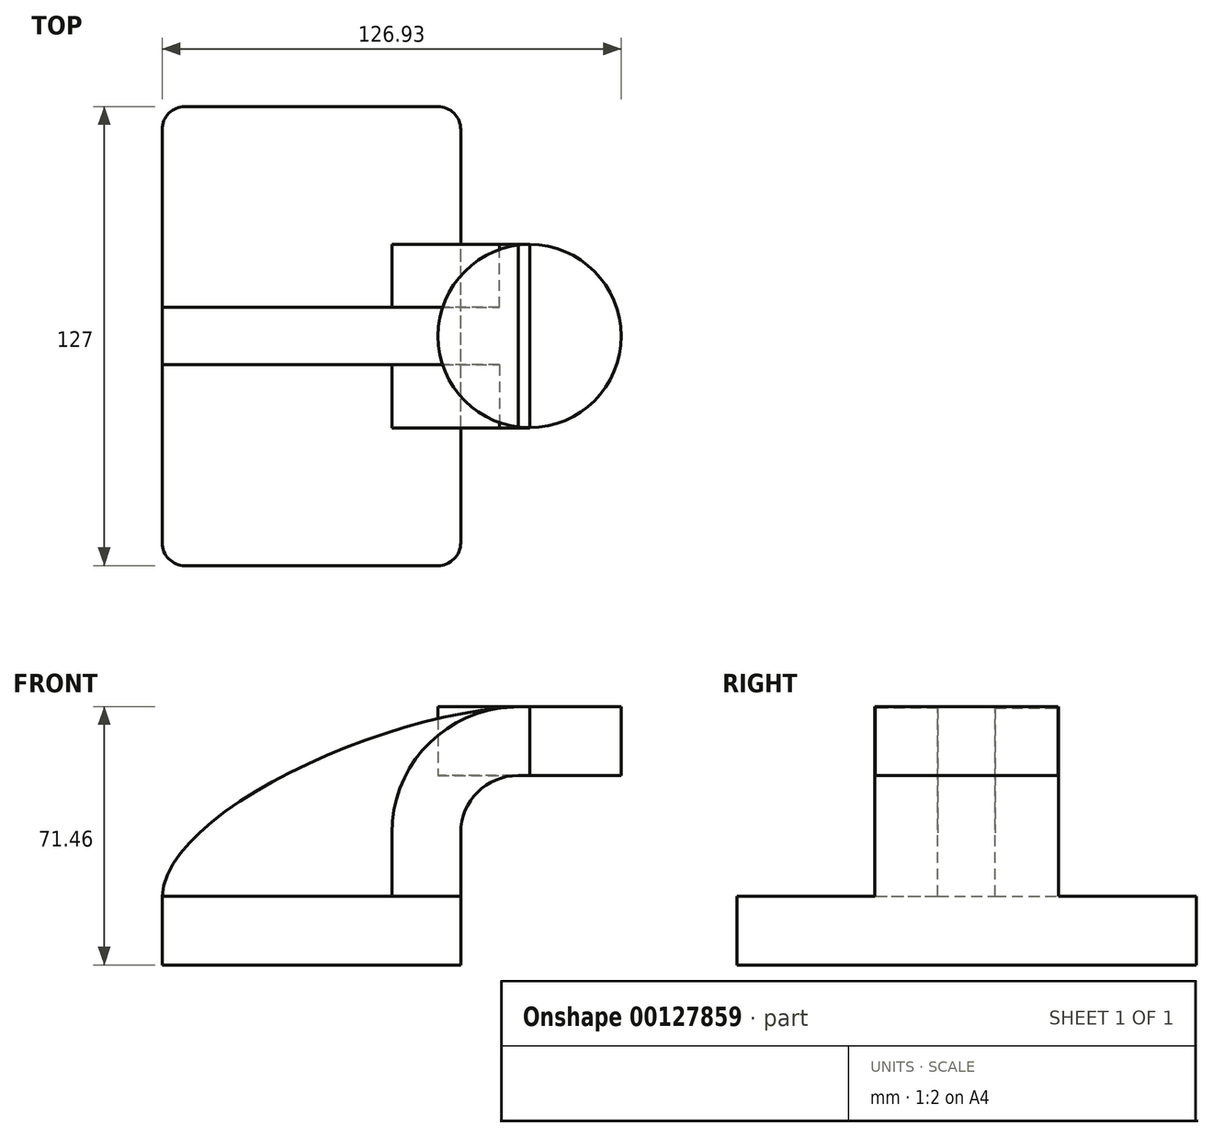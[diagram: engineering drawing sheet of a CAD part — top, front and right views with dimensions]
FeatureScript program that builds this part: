
annotation { "Feature Type Name" : "Feature", "Feature Type Description" : "" }
export const myFeature = defineFeature(function(context is Context, id is Id, definition is map)
    precondition{}
    {
        {
            var Q0;
            Q0=qCreatedBy(makeId("Front.planeOp"),FACE);
            var sketch = newSketch(context, id + "F0", { "sketchPlane" : qUnion([Q0])});
            skLineSegment(sketch, "E0.bottom", {"start": v(111.12, 38.1) * mm, "end": v(60.33, 38.1) * mm});
            skLineSegment(sketch, "E0.top", {"start": v(111.12, 66.68) * mm, "end": v(60.33, 66.68) * mm});
            skLineSegment(sketch, "E0.left", {"start": v(111.12, 38.1) * mm, "end": v(111.12, 66.68) * mm});
            skLineSegment(sketch, "E0.right", {"start": v(60.33, 38.1) * mm, "end": v(60.33, 66.68) * mm});
            skPoint(sketch, "E0.middle", {"position": v(85.72, 52.39) * mm});
            skLineSegment(sketch, "E1.bottom", {"start": v(41.28, -9.52) * mm, "end": v(-41.28, -9.53) * mm});
            skLineSegment(sketch, "E1.top", {"start": v(41.28, 9.53) * mm, "end": v(-41.28, 9.52) * mm});
            skLineSegment(sketch, "E1.left", {"start": v(41.28, -9.52) * mm, "end": v(41.28, 9.53) * mm});
            skLineSegment(sketch, "E1.right", {"start": v(-41.28, -9.53) * mm, "end": v(-41.28, 9.52) * mm});
            skPoint(sketch, "E1.middle", {"position": v(0, 0) * mm});
            skLineSegment(sketch, "E2", {"start": v(41.28, 9.53) * mm, "end": v(41.28, 27) * mm});
            skArc(sketch, "E3", {"start": v(41.28, 27) * mm, "mid": v(45.92, 38.23) * mm, "end": v(57.15, 42.88) * mm});
            skArc(sketch, "E4.1", {"start": v(22.23, 27) * mm, "mid": v(32.45, 51.7) * mm, "end": v(57.15, 61.93) * mm});
            skLineSegment(sketch, "E4.2", {"start": v(22.23, 9.53) * mm, "end": v(22.23, 27) * mm});
            skLineSegment(sketch, "E5", {"start": v(57.15, 42.88) * mm, "end": v(85.65, 42.88) * mm});
            skLineSegment(sketch, "E6", {"start": v(57.15, 61.93) * mm, "end": v(85.65, 61.93) * mm});
            skLineSegment(sketch, "E7", {"start": v(85.65, 61.93) * mm, "end": v(85.65, 42.88) * mm});
            skFitSpline(sketch, "E8", {"points": [v(-41.28, 9.53) * mm, v(57.15, 61.93) * mm], "startDerivative": vector(2.82, 69.45) * mm, "endDerivative": vector(112.7, 5.21) * mm});
            skSolve(sketch);
        }
        {
            var Q0;
            Q0=makeQuery(id+"F0.imprint","IMPRINT",FACE,{"disambiguationData":[TD([[makeQuery(id+"F0.imprint","IMPRINT",EDGE,{"derivedFrom":sQuery(id+"F0.wireOp",EDGE,"E1.bottom")}),-1.0]])]});
            extrude(context, id + "F1", {"entities" : qUnion([Q0]), "endBound" : BoundingType.SYMMETRIC, "depth" : 127 * mm});
        }
        {
            var Q0;
            {var subQ4=sQuery(id+"F0.wireOp",EDGE,"E2");Q0=makeQuery(id+"F0.imprint","IMPRINT",FACE,{"disambiguationData":[TD([[makeQuery(id+"F0.imprint","IMPRINT",EDGE,{"derivedFrom":subQ4}),1.0]])]});}
            extrude(context, id + "F2", {"entities" : qUnion([Q0]), "operationType" : NewBodyOperationType.ADD, "endBound" : BoundingType.SYMMETRIC, "depth" : 50.8 * mm});
        }
        {
            var Q0;
            {var subQ3=sQuery(id+"F0.wireOp",EDGE,"E4.2");Q0=makeQuery(id+"F0.imprint","IMPRINT",FACE,{"disambiguationData":[TD([[makeQuery(id+"F0.imprint","IMPRINT",EDGE,{"derivedFrom":subQ3}),1.0]])]});}
            extrude(context, id + "F3", {"entities" : qUnion([Q0]), "operationType" : NewBodyOperationType.ADD, "endBound" : BoundingType.SYMMETRIC, "depth" : 15.88 * mm});
        }
        {
            var Q0;
            {var subQ5=sQuery(id+"F0.wireOp",EDGE,"E7");Q0=makeQuery(id+"F0.imprint","IMPRINT",FACE,{"disambiguationData":[TD([[makeQuery(id+"F0.imprint","IMPRINT",EDGE,{"derivedFrom":subQ5}),-1.0]])]});}
            var Q1;
            Q1=sQuery(id+"F0.wireOp",EDGE,"E0.right");
            revolve(context, id + "F4", {"entities" : qUnion([Q0]), "axis" : qUnion([Q1]), "revolveType" : RevolveType.FULL});
        }
        {
            var Q0;
            Q0=makeQuery(id+"F1.opExtrude","CAP_EDGE",EDGE,{"disambiguationData":[OSD([sQuery(id+"F0.wireOp",EDGE,"E1.left")])],"isStart":true});
            var Q1;
            Q1=makeQuery(id+"F1.opExtrude","CAP_EDGE",EDGE,{"disambiguationData":[OSD([sQuery(id+"F0.wireOp",EDGE,"E1.left")])],"isStart":false});
            var Q2;
            Q2=makeQuery(id+"F1.opExtrude","CAP_EDGE",EDGE,{"disambiguationData":[OSD([sQuery(id+"F0.wireOp",EDGE,"E1.right")])],"isStart":false});
            var Q3;
            Q3=makeQuery(id+"F1.opExtrude","CAP_EDGE",EDGE,{"disambiguationData":[OSD([sQuery(id+"F0.wireOp",EDGE,"E1.right")])],"isStart":true});
            fillet(context, id + "F5", {"entities" : qUnion([Q0, Q1, Q2, Q3]), "radius" : 6.35 * mm, "tangentPropagation" : true, "allowEdgeOverflow" : false});
        }
    });
